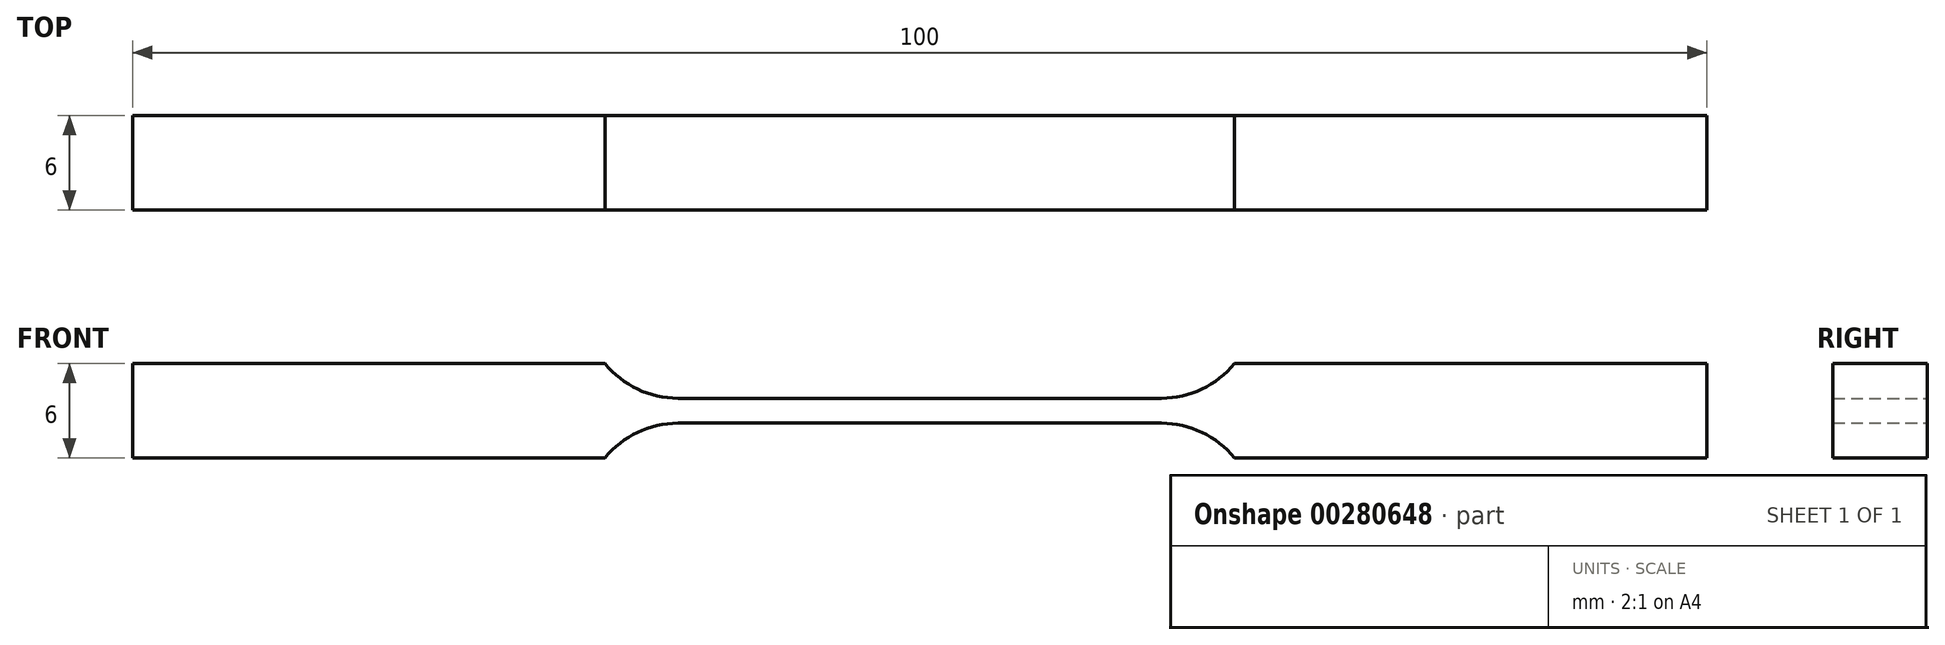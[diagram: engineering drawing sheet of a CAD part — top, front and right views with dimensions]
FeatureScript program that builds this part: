
annotation { "Feature Type Name" : "Feature", "Feature Type Description" : "" }
export const myFeature = defineFeature(function(context is Context, id is Id, definition is map)
    precondition{}
    {
        {
            var Q0;
            Q0=qCreatedBy(makeId("Front.planeOp"),FACE);
            var sketch = newSketch(context, id + "F0", { "sketchPlane" : qUnion([Q0])});
            skLineSegment(sketch, "E0", {"start": v(0, 0.8) * mm, "end": v(15.35, 0.8) * mm});
            skArc(sketch, "E1", {"start": v(15.35, 0.8) * mm, "mid": v(17.92, 1.37) * mm, "end": v(20, 3) * mm});
            skLineSegment(sketch, "E2", {"start": v(20, 3) * mm, "end": v(50, 3) * mm});
            skLineSegment(sketch, "E3", {"start": v(50, 3) * mm, "end": v(50, 0) * mm});
            skLineSegment(sketch, "E4.MirrorCS", {"start": v(0, -0.8) * mm, "end": v(15.35, -0.8) * mm});
            skLineSegment(sketch, "E5.MirrorCS", {"start": v(50, -3) * mm, "end": v(50, 0) * mm});
            skLineSegment(sketch, "E6.MirrorCS", {"start": v(20, -3) * mm, "end": v(50, -3) * mm});
            skArc(sketch, "E7.MirrorCS", {"start": v(15.35, -0.8) * mm, "mid": v(17.92, -1.37) * mm, "end": v(20, -3) * mm});
            skArc(sketch, "E8.MirrorCS", {"start": v(-15.35, -0.8) * mm, "mid": v(-17.92, -1.37) * mm, "end": v(-20, -3) * mm});
            skLineSegment(sketch, "E9.MirrorCS", {"start": v(-20, -3) * mm, "end": v(-50, -3) * mm});
            skLineSegment(sketch, "E10.MirrorCS", {"start": v(0, 0.8) * mm, "end": v(-15.35, 0.8) * mm});
            skArc(sketch, "E11.MirrorCS", {"start": v(-15.35, 0.8) * mm, "mid": v(-17.92, 1.37) * mm, "end": v(-20, 3) * mm});
            skLineSegment(sketch, "E12.MirrorCS", {"start": v(-20, 3) * mm, "end": v(-50, 3) * mm});
            skLineSegment(sketch, "E13.MirrorCS", {"start": v(-50, -3) * mm, "end": v(-50, 0) * mm});
            skLineSegment(sketch, "E14.MirrorCS", {"start": v(-50, 3) * mm, "end": v(-50, 0) * mm});
            skLineSegment(sketch, "E15.MirrorCS", {"start": v(0, -0.8) * mm, "end": v(-15.35, -0.8) * mm});
            skSolve(sketch);
        }
        {
            var Q0;
            Q0 = qSketchRegion(id + "F0", true);
            extrude(context, id + "F1", {"entities" : qUnion([Q0]), "endBound" : BoundingType.SYMMETRIC, "depth" : 6 * mm});
        }
    });
